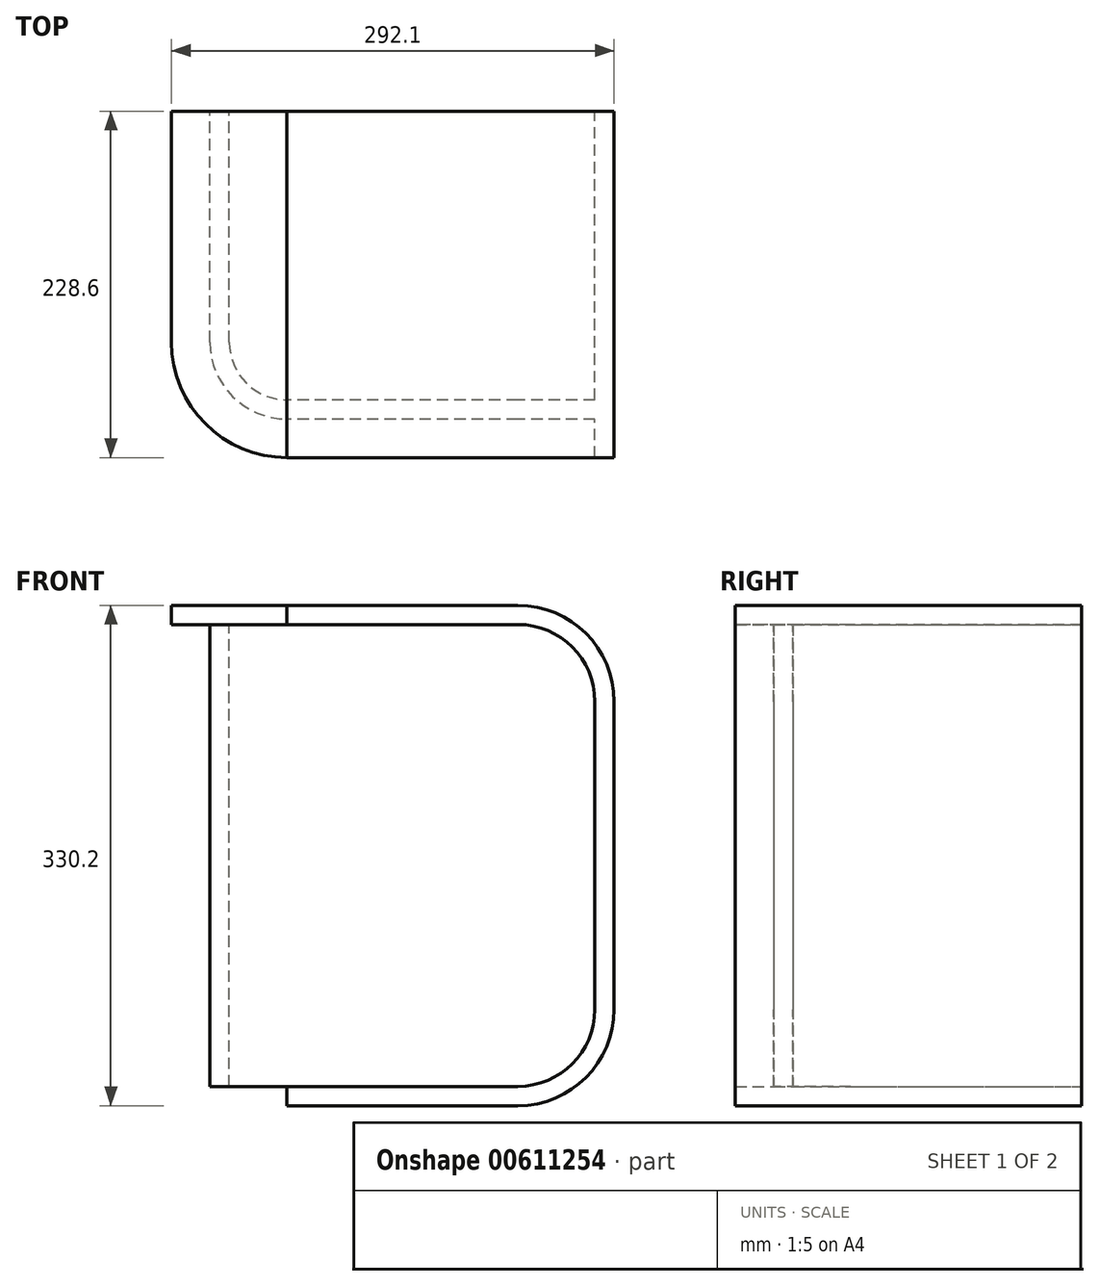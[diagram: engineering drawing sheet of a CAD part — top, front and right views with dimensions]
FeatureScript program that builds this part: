
annotation { "Feature Type Name" : "Feature", "Feature Type Description" : "" }
export const myFeature = defineFeature(function(context is Context, id is Id, definition is map)
    precondition{}
    {
        {
            var Q0;
            Q0=qCreatedBy(makeId("Front.planeOp"),FACE);
            var sketch = newSketch(context, id + "F0", { "sketchPlane" : qUnion([Q0])});
            skLineSegment(sketch, "E0.bottom", {"start": v(50.8, 152.4) * mm, "end": v(-101.6, 152.4) * mm});
            skLineSegment(sketch, "E0.top", {"start": v(50.8, -152.4) * mm, "end": v(-101.6, -152.4) * mm});
            skLineSegment(sketch, "E0.left", {"start": v(101.6, 101.6) * mm, "end": v(101.6, -101.6) * mm});
            skLineSegment(sketch, "E0.right", {"start": v(-101.6, 152.4) * mm, "end": v(-101.6, -152.4) * mm});
            skPoint(sketch, "E0.middle", {"position": v(0, 0) * mm});
            skPoint(sketch, "E1.visualSharp", {"position": v(101.6, 152.4) * mm});
            skArc(sketch, "E1.filletArc", {"start": v(101.6, 101.6) * mm, "mid": v(86.72, 137.52) * mm, "end": v(50.8, 152.4) * mm});
            skPoint(sketch, "E2.visualSharp", {"position": v(101.6, -152.4) * mm});
            skArc(sketch, "E2.filletArc", {"start": v(50.8, -152.4) * mm, "mid": v(86.72, -137.52) * mm, "end": v(101.6, -101.6) * mm});
            skSolve(sketch);
        }
        {
            var Q0;
            Q0 = qSketchRegion(id + "F0", true);
            extrude(context, id + "F1", {"entities" : qUnion([Q0]), "depth" : 12.7 * mm, "offsetDistance" : 25.4 * mm});
        }
        {
            var Q0;
            Q0=makeQuery(id+"F1.opExtrude","SWEPT_FACE",FACE,{"disambiguationData":[OSD([sQuery(id+"F0.wireOp",EDGE,"E0.bottom")])]});
            var sketch = newSketch(context, id + "F2", { "sketchPlane" : qUnion([Q0])});
            skLineSegment(sketch, "E3.top", {"start": v(-101.6, 203.2) * mm, "end": v(-88.9, 203.2) * mm});
            skArc(sketch, "E4", {"start": v(-152.4, 38.1) * mm, "mid": v(-137.52, 2.18) * mm, "end": v(-101.6, -12.7) * mm});
            skArc(sketch, "E5.0", {"start": v(-139.7, 38.1) * mm, "mid": v(-128.54, 11.16) * mm, "end": v(-101.6, 0) * mm});
            skLineSegment(sketch, "E6", {"start": v(-152.4, 38.1) * mm, "end": v(-152.4, 190.5) * mm});
            skLineSegment(sketch, "E7", {"start": v(-139.7, 38.1) * mm, "end": v(-139.7, 190.5) * mm});
            skLineSegment(sketch, "E8", {"start": v(-139.7, 190.5) * mm, "end": v(-152.4, 190.5) * mm});
            skSolve(sketch);
        }
        {
            var Q0;
            Q0 = qSketchRegion(id + "F2", true);
            var Q1;
            Q1=makeQuery(id+"F2.imprint","IMPRINT",FACE,{"disambiguationData":[TD([[makeQuery(id+"F2.imprint","IMPRINT",EDGE,{"derivedFrom":sQuery(id+"F2.wireOp",EDGE,"E4")}),1.0]])]});
            extrude(context, id + "F3", {"entities" : qUnion([Q0, Q1]), "depth" : -304.8 * mm, "offsetDistance" : 25.4 * mm});
        }
        {
            var Q0;
            Q0=makeQuery(id+"F1.opExtrude","CAP_FACE",FACE,{"disambiguationData":[OSD([sQuery(id+"F0.wireOp",EDGE,"E0.bottom"),sQuery(id+"F0.wireOp",EDGE,"E0.top"),sQuery(id+"F0.wireOp",EDGE,"E0.left"),sQuery(id+"F0.wireOp",EDGE,"E0.right"),sQuery(id+"F0.wireOp",EDGE,"E1.filletArc"),sQuery(id+"F0.wireOp",EDGE,"E2.filletArc")])],"isStart":false});
            var sketch = newSketch(context, id + "F4", { "sketchPlane" : qUnion([Q0])});
            skLineSegment(sketch, "E9.0", {"start": v(50.8, 165.1) * mm, "end": v(-101.6, 165.1) * mm});
            skArc(sketch, "E10.0", {"start": v(114.3, 101.6) * mm, "mid": v(95.7, 146.5) * mm, "end": v(50.8, 165.1) * mm});
            skLineSegment(sketch, "E11.0", {"start": v(114.3, 101.6) * mm, "end": v(114.3, -101.6) * mm});
            skArc(sketch, "E12.0", {"start": v(50.8, -165.1) * mm, "mid": v(95.7, -146.5) * mm, "end": v(114.3, -101.6) * mm});
            skLineSegment(sketch, "E13.0", {"start": v(50.8, -165.1) * mm, "end": v(-101.6, -165.1) * mm});
            skLineSegment(sketch, "E14", {"start": v(-101.6, 165.1) * mm, "end": v(-101.6, 152.4) * mm});
            skLineSegment(sketch, "E15", {"start": v(-101.6, -165.1) * mm, "end": v(-101.6, -152.4) * mm});
            skSolve(sketch);
        }
        {
            var Q0;
            Q0=makeQuery(id+"F4.imprint","IMPRINT",FACE,{"disambiguationData":[TD([[makeQuery(id+"F4.imprint","IMPRINT",EDGE,{"derivedFrom":sQuery(id+"F4.wireOp",EDGE,"E9.0")}),1.0]])]});
            extrude(context, id + "F5", {"entities" : qUnion([Q0]), "operationType" : NewBodyOperationType.ADD, "depth" : 25.4 * mm, "offsetDistance" : 25.4 * mm, "hasSecondDirection" : true, "secondDirectionOppositeDirection" : true, "secondDirectionDepth" : 203.2 * mm});
        }
        {
            var Q0;
            Q0=makeQuery(id+"F2.imprint","IMPRINT",FACE,{"disambiguationData":[TD([[makeQuery(id+"F2.imprint","IMPRINT",EDGE,{"derivedFrom":sQuery(id+"F2.wireOp",EDGE,"E4")}),1.0]])]});
            var sketch = newSketch(context, id + "F6", { "sketchPlane" : qUnion([Q0])});
            skArc(sketch, "E16.0", {"start": v(-177.8, 38.1) * mm, "mid": v(-155.48, -15.78) * mm, "end": v(-101.6, -38.1) * mm});
            skLineSegment(sketch, "E17", {"start": v(-177.8, 38.1) * mm, "end": v(-177.8, 190.5) * mm});
            skLineSegment(sketch, "E18", {"start": v(-177.8, 190.5) * mm, "end": v(-101.6, 190.5) * mm});
            skLineSegment(sketch, "E19", {"start": v(-101.6, 190.5) * mm, "end": v(-101.6, -38.1) * mm});
            skSolve(sketch);
        }
        {
            var Q0;
            Q0 = qSketchRegion(id + "F6", true);
            extrude(context, id + "F7", {"entities" : qUnion([Q0]), "depth" : 12.7 * mm, "offsetDistance" : 25.4 * mm});
        }
    });
